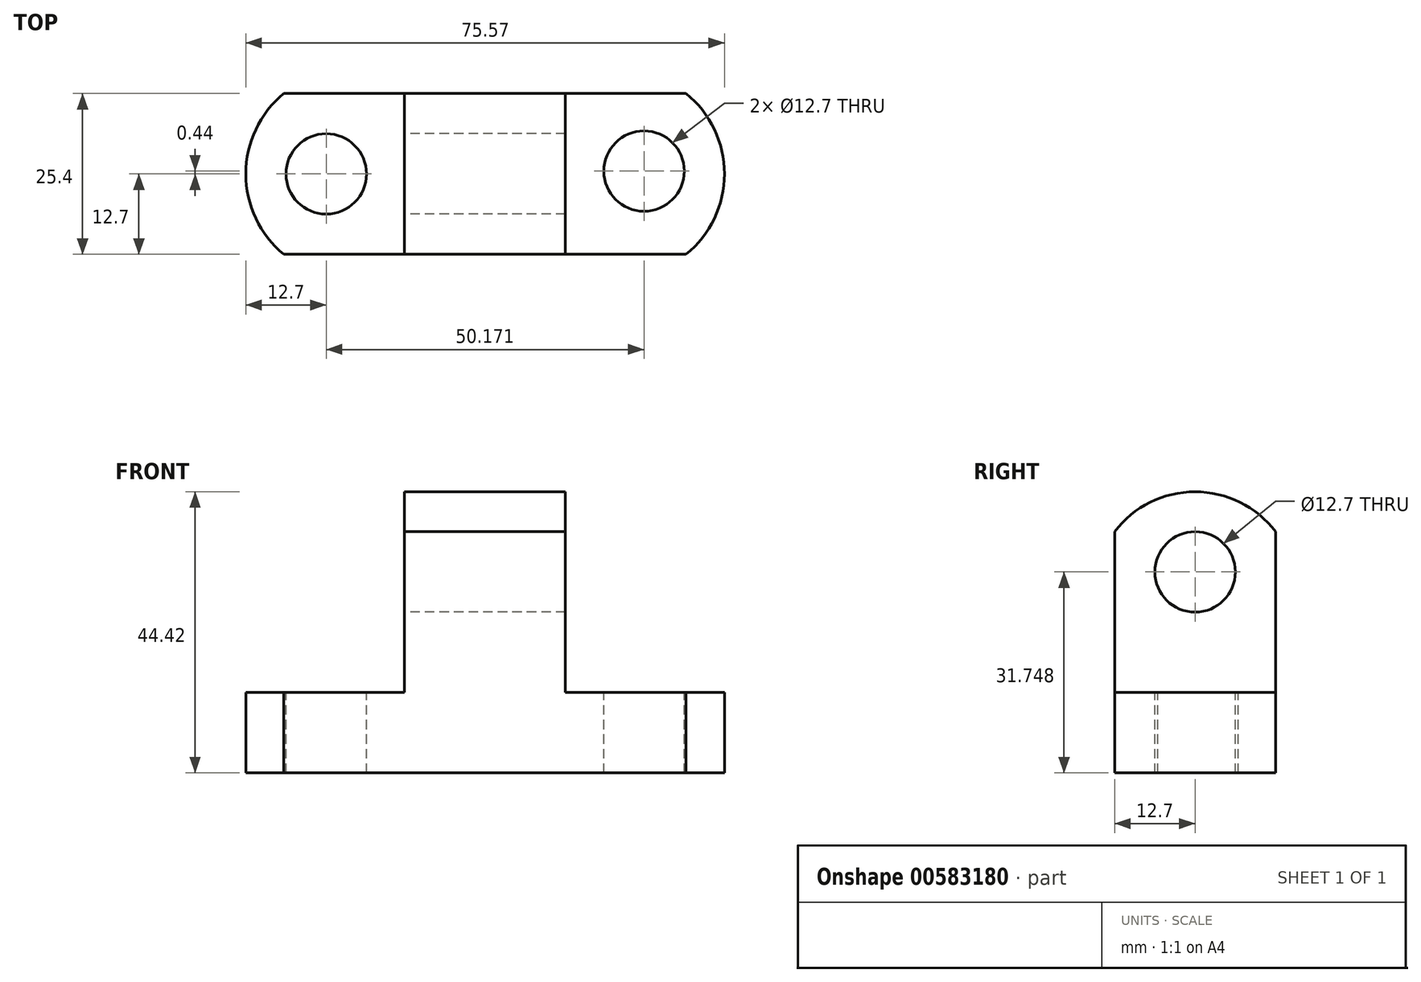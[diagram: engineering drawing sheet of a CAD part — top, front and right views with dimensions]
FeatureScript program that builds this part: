
annotation { "Feature Type Name" : "Feature", "Feature Type Description" : "" }
export const myFeature = defineFeature(function(context is Context, id is Id, definition is map)
    precondition{}
    {
        {
            var Q0;
            Q0=qCreatedBy(makeId("Front.planeOp"),FACE);
            var sketch = newSketch(context, id + "F0", { "sketchPlane" : qUnion([Q0])});
            skLineSegment(sketch, "E0.bottom", {"start": v(0, 0) * mm, "end": v(-76.2, 0) * mm});
            skLineSegment(sketch, "E0.top", {"start": v(0, 44.45) * mm, "end": v(-76.2, 44.45) * mm});
            skLineSegment(sketch, "E0.left", {"start": v(0, 0) * mm, "end": v(0, 44.45) * mm});
            skLineSegment(sketch, "E0.right", {"start": v(-76.2, 0) * mm, "end": v(-76.2, 44.45) * mm});
            skSolve(sketch);
        }
        {
            var Q0;
            Q0=makeQuery(id+"F0.imprint","IMPRINT",FACE,{"disambiguationData":[TD([[makeQuery(id+"F0.imprint","IMPRINT",EDGE,{"derivedFrom":sQuery(id+"F0.wireOp",EDGE,"E0.bottom")}),-1.0]])]});
            extrude(context, id + "F1", {"entities" : qUnion([Q0]), "depth" : 25.4 * mm, "offsetDistance" : 25.4 * mm});
        }
        {
            var Q0;
            Q0=makeQuery(id+"F1.opExtrude","CAP_FACE",FACE,{"disambiguationData":[OSD([sQuery(id+"F0.wireOp",EDGE,"E0.bottom"),sQuery(id+"F0.wireOp",EDGE,"E0.top"),sQuery(id+"F0.wireOp",EDGE,"E0.left"),sQuery(id+"F0.wireOp",EDGE,"E0.right")])],"isStart":false});
            var sketch = newSketch(context, id + "F2", { "sketchPlane" : qUnion([Q0])});
            skLineSegment(sketch, "E1", {"start": v(0, 12.7) * mm, "end": v(-25.4, 12.7) * mm});
            skLineSegment(sketch, "E2", {"start": v(-25.4, 12.7) * mm, "end": v(-25.4, 0) * mm});
            skLineSegment(sketch, "E3", {"start": v(-25.4, 12.7) * mm, "end": v(-25.4, 44.45) * mm});
            skLineSegment(sketch, "E4", {"start": v(-76.2, 12.7) * mm, "end": v(-50.8, 12.7) * mm});
            skLineSegment(sketch, "E5", {"start": v(-50.8, 12.7) * mm, "end": v(-50.8, 0) * mm});
            skLineSegment(sketch, "E6", {"start": v(-50.8, 0) * mm, "end": v(-50.8, 44.45) * mm});
            skSolve(sketch);
        }
        {
            var Q0;
            {var subQ0=sQuery(id+"F2.wireOp",EDGE,"E4");Q0=makeQuery(id+"F2.imprint","IMPRINT",FACE,{"disambiguationData":[TD([[makeQuery(id+"F2.imprint","IMPRINT",EDGE,{"derivedFrom":subQ0}),1.0]])]});}
            var Q1;
            {var subQ0=sQuery(id+"F2.wireOp",EDGE,"E1");Q1=makeQuery(id+"F2.imprint","IMPRINT",FACE,{"disambiguationData":[TD([[makeQuery(id+"F2.imprint","IMPRINT",EDGE,{"derivedFrom":subQ0}),-1.0]])]});}
            extrude(context, id + "F3", {"entities" : qUnion([Q0, Q1]), "operationType" : NewBodyOperationType.REMOVE, "endBound" : BoundingType.THROUGH_ALL, "oppositeDirection" : true, "depth" : 25.4 * mm, "offsetDistance" : 25.4 * mm});
        }
        {
            var Q0;
            Q0=makeQuery(id+"F3.boolean.opBoolean","COPY",FACE,{"derivedFrom":makeQuery(id+"F3.opExtrude","SWEPT_FACE",FACE,{"disambiguationData":[OSD([sQuery(id+"F2.wireOp",EDGE,"E3")])]})});
            var sketch = newSketch(context, id + "F4", { "sketchPlane" : qUnion([Q0])});
            skLineSegment(sketch, "E7", {"start": v(-25.4, 12.7) * mm, "end": v(-25.4, 38.11) * mm});
            skArc(sketch, "E8", {"start": v(0, 38.11) * mm, "mid": v(-12.7, 44.42) * mm, "end": v(-25.4, 38.11) * mm});
            skSolve(sketch);
        }
        {
            var Q0;
            {var subQ0=sQuery(id+"F4.wireOp",EDGE,"E8");Q0=makeQuery(id+"F4.imprint","IMPRINT",FACE,{"disambiguationData":[TD([[makeQuery(id+"F4.imprint","IMPRINT",EDGE,{"derivedFrom":subQ0}),-1.0]])]});}
            extrude(context, id + "F5", {"entities" : qUnion([Q0]), "operationType" : NewBodyOperationType.REMOVE, "endBound" : BoundingType.THROUGH_ALL, "oppositeDirection" : true, "depth" : 25.4 * mm, "offsetDistance" : 25.4 * mm});
        }
        {
            var Q0;
            Q0=makeQuery(id+"F3.boolean.opBoolean","COPY",FACE,{"derivedFrom":makeQuery(id+"F3.opExtrude","SWEPT_FACE",FACE,{"disambiguationData":[OSD([sQuery(id+"F2.wireOp",EDGE,"E1")])]})});
            var sketch = newSketch(context, id + "F6", { "sketchPlane" : qUnion([Q0])});
            skLineSegment(sketch, "E9", {"start": v(-25.4, 0) * mm, "end": v(-6.35, 0) * mm});
            skArc(sketch, "E10", {"start": v(-6.35, -25.4) * mm, "mid": v(-0.3, -12.7) * mm, "end": v(-6.35, 0) * mm});
            skSolve(sketch);
        }
        {
            var Q0;
            {var subQ0=sQuery(id+"F6.wireOp",EDGE,"E10");Q0=makeQuery(id+"F6.imprint","IMPRINT",FACE,{"disambiguationData":[TD([[makeQuery(id+"F6.imprint","IMPRINT",EDGE,{"derivedFrom":subQ0}),-1.0]])]});}
            extrude(context, id + "F7", {"entities" : qUnion([Q0]), "operationType" : NewBodyOperationType.REMOVE, "endBound" : BoundingType.THROUGH_ALL, "oppositeDirection" : true, "depth" : 25.4 * mm, "offsetDistance" : 25.4 * mm});
        }
        {
            var Q0;
            Q0=makeQuery(id+"F3.boolean.opBoolean","COPY",FACE,{"derivedFrom":makeQuery(id+"F3.opExtrude","SWEPT_FACE",FACE,{"disambiguationData":[OSD([sQuery(id+"F2.wireOp",EDGE,"E4")])]})});
            var sketch = newSketch(context, id + "F8", { "sketchPlane" : qUnion([Q0])});
            skLineSegment(sketch, "E11", {"start": v(-50.8, -25.4) * mm, "end": v(-69.85, -25.4) * mm});
            skArc(sketch, "E12", {"start": v(-69.85, 0) * mm, "mid": v(-75.87, -12.7) * mm, "end": v(-69.85, -25.4) * mm});
            skSolve(sketch);
        }
        {
            var Q0;
            {var subQ0=sQuery(id+"F8.wireOp",EDGE,"E12");Q0=makeQuery(id+"F8.imprint","IMPRINT",FACE,{"disambiguationData":[TD([[makeQuery(id+"F8.imprint","IMPRINT",EDGE,{"derivedFrom":subQ0}),-1.0]])]});}
            extrude(context, id + "F9", {"entities" : qUnion([Q0]), "operationType" : NewBodyOperationType.REMOVE, "endBound" : BoundingType.THROUGH_ALL, "oppositeDirection" : true, "depth" : 25.4 * mm, "offsetDistance" : 25.4 * mm});
        }
        {
            var Q0;
            Q0=makeQuery(id+"F3.boolean.opBoolean","COPY",FACE,{"derivedFrom":makeQuery(id+"F3.opExtrude","SWEPT_FACE",FACE,{"disambiguationData":[OSD([sQuery(id+"F2.wireOp",EDGE,"E6")])]})});
            var sketch = newSketch(context, id + "F10", { "sketchPlane" : qUnion([Q0])});
            skLineSegment(sketch, "E13", {"start": v(12.7, 12.7) * mm, "end": v(12.7, 25.4) * mm});
            skCircle(sketch, "E14", {"center": v(12.7, 31.75) * mm, "radius": 6.35 * mm});
            skSolve(sketch);
        }
        {
            var Q0;
            Q0=makeQuery(id+"F10.imprint","IMPRINT",FACE,{"disambiguationData":[TD([[makeQuery(id+"F10.imprint","IMPRINT",EDGE,{"derivedFrom":sQuery(id+"F10.wireOp",EDGE,"E14")}),1.0]])]});
            extrude(context, id + "F11", {"entities" : qUnion([Q0]), "operationType" : NewBodyOperationType.REMOVE, "endBound" : BoundingType.THROUGH_ALL, "oppositeDirection" : true, "depth" : 25.4 * mm, "offsetDistance" : 25.4 * mm});
        }
        {
            var Q0;
            Q0=makeQuery(id+"F3.boolean.opBoolean","COPY",FACE,{"derivedFrom":makeQuery(id+"F3.opExtrude","SWEPT_FACE",FACE,{"disambiguationData":[OSD([sQuery(id+"F2.wireOp",EDGE,"E4")])]})});
            var sketch = newSketch(context, id + "F12", { "sketchPlane" : qUnion([Q0])});
            skLineSegment(sketch, "E15", {"start": v(-75.87, -12.7) * mm, "end": v(-69.52, -12.7) * mm});
            skCircle(sketch, "E16", {"center": v(-63.17, -12.7) * mm, "radius": 6.35 * mm});
            skSolve(sketch);
        }
        {
            var Q0;
            Q0=makeQuery(id+"F12.imprint","IMPRINT",FACE,{"disambiguationData":[TD([[makeQuery(id+"F12.imprint","IMPRINT",EDGE,{"derivedFrom":sQuery(id+"F12.wireOp",EDGE,"E16")}),1.0]])]});
            extrude(context, id + "F13", {"entities" : qUnion([Q0]), "operationType" : NewBodyOperationType.REMOVE, "endBound" : BoundingType.THROUGH_ALL, "oppositeDirection" : true, "depth" : 25.4 * mm, "offsetDistance" : 25.4 * mm});
        }
        {
            var Q0;
            Q0=makeQuery(id+"F3.boolean.opBoolean","COPY",FACE,{"derivedFrom":makeQuery(id+"F3.opExtrude","SWEPT_FACE",FACE,{"disambiguationData":[OSD([sQuery(id+"F2.wireOp",EDGE,"E1")])]})});
            var sketch = newSketch(context, id + "F14", { "sketchPlane" : qUnion([Q0])});
            skCircle(sketch, "E17", {"center": v(-13, -12.26) * mm, "radius": 6.35 * mm});
            skSolve(sketch);
        }
        {
            var Q0;
            Q0=makeQuery(id+"F14.imprint","IMPRINT",FACE,{"disambiguationData":[TD([[makeQuery(id+"F14.imprint","IMPRINT",EDGE,{"derivedFrom":sQuery(id+"F14.wireOp",EDGE,"E17")}),1.0]])]});
            extrude(context, id + "F15", {"entities" : qUnion([Q0]), "operationType" : NewBodyOperationType.REMOVE, "endBound" : BoundingType.THROUGH_ALL, "oppositeDirection" : true, "depth" : 25.4 * mm, "offsetDistance" : 25.4 * mm});
        }
    });
